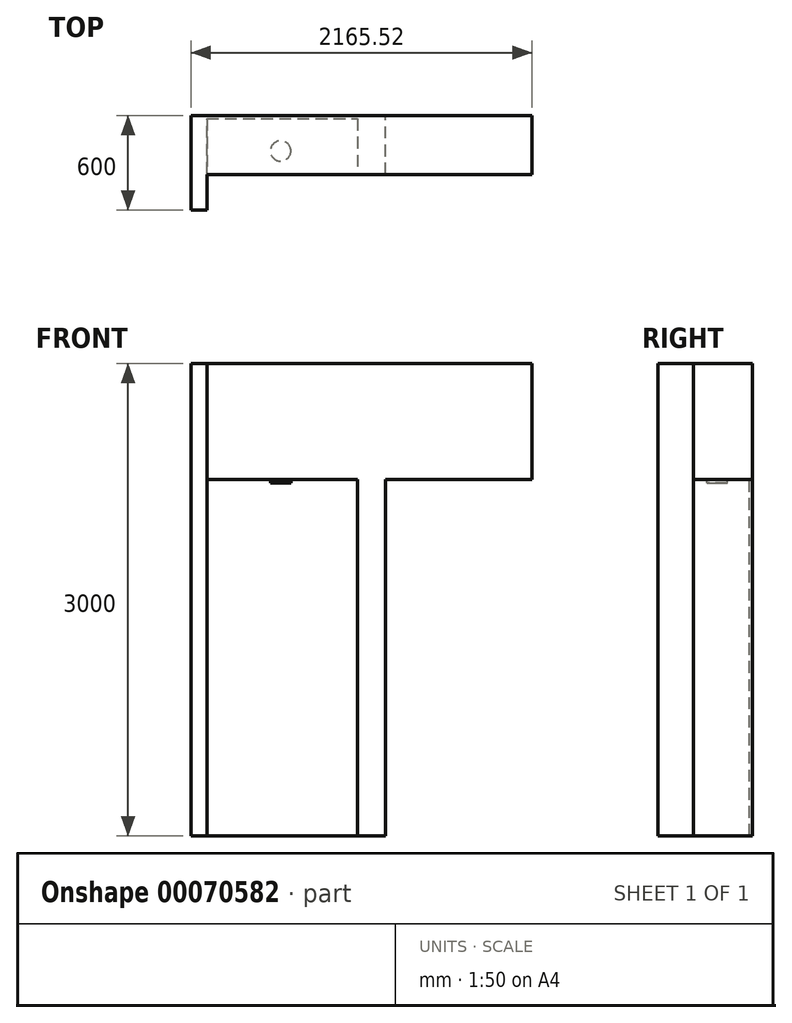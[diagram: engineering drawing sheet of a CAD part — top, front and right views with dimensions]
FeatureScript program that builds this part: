
annotation { "Feature Type Name" : "Feature", "Feature Type Description" : "" }
export const myFeature = defineFeature(function(context is Context, id is Id, definition is map)
    precondition{}
    {
        {
            var Q0;
            Q0=qCreatedBy(makeId("Front.planeOp"),FACE);
            var sketch = newSketch(context, id + "F0", { "sketchPlane" : qUnion([Q0])});
            skLineSegment(sketch, "E0.bottom", {"start": v(-617.5, 0) * mm, "end": v(617.5, 0) * mm});
            skLineSegment(sketch, "E0.top", {"start": v(-617.5, 3000) * mm, "end": v(1548.02, 3000) * mm});
            skLineSegment(sketch, "E0.left", {"start": v(-617.5, 0) * mm, "end": v(-617.5, 3000) * mm});
            skLineSegment(sketch, "E0.right", {"start": v(617.5, 0) * mm, "end": v(617.5, 2263) * mm});
            skLineSegment(sketch, "E1", {"start": v(617.5, 2263) * mm, "end": v(1548.02, 2263) * mm});
            skLineSegment(sketch, "E2", {"start": v(1548.02, 2263) * mm, "end": v(1548.02, 3000) * mm});
            skSolve(sketch);
        }
        {
            var Q0;
            Q0=makeQuery(id+"F0.imprint","IMPRINT",FACE,{"disambiguationData":[TD([[makeQuery(id+"F0.imprint","IMPRINT",EDGE,{"derivedFrom":sQuery(id+"F0.wireOp",EDGE,"E0.bottom")}),1.0]])]});
            extrude(context, id + "F1", {"entities" : qUnion([Q0]), "depth" : 600 * mm});
        }
        {
            var Q0;
            Q0=makeQuery(id+"F1.opExtrude","SWEPT_FACE",FACE,{"disambiguationData":[OSD([sQuery(id+"F0.wireOp",EDGE,"E0.top")])]});
            var sketch = newSketch(context, id + "F2", { "sketchPlane" : qUnion([Q0])});
            skLineSegment(sketch, "E3.bottom", {"start": v(-517.5, -600) * mm, "end": v(1548.02, -600) * mm});
            skLineSegment(sketch, "E3.top", {"start": v(-517.5, -374.12) * mm, "end": v(1548.02, -374.12) * mm});
            skLineSegment(sketch, "E3.left", {"start": v(-517.5, -600) * mm, "end": v(-517.5, -374.12) * mm});
            skLineSegment(sketch, "E3.right", {"start": v(1548.02, -600) * mm, "end": v(1548.02, -374.12) * mm});
            skSolve(sketch);
        }
        {
            var Q0;
            Q0=makeQuery(id+"F2.imprint","IMPRINT",FACE,{"disambiguationData":[TD([[makeQuery(id+"F2.imprint","IMPRINT",EDGE,{"derivedFrom":sQuery(id+"F2.wireOp",EDGE,"E3.bottom")}),1.0]])]});
            extrude(context, id + "F3", {"entities" : qUnion([Q0]), "operationType" : NewBodyOperationType.REMOVE, "oppositeDirection" : true, "depth" : 4000 * mm});
        }
        {
            var Q0;
            Q0=makeQuery(id+"F3.boolean.opBoolean","COPY",FACE,{"derivedFrom":makeQuery(id+"F3.opExtrude","SWEPT_FACE",FACE,{"disambiguationData":[OSD([sQuery(id+"F2.wireOp",EDGE,"E3.top")])]})});
            var sketch = newSketch(context, id + "F4", { "sketchPlane" : qUnion([Q0])});
            skLineSegment(sketch, "E4.bottom", {"start": v(-517.5, 0) * mm, "end": v(440.5, 0) * mm});
            skLineSegment(sketch, "E4.top", {"start": v(-517.5, 2263) * mm, "end": v(440.5, 2263) * mm});
            skLineSegment(sketch, "E4.left", {"start": v(-517.5, 0) * mm, "end": v(-517.5, 2263) * mm});
            skLineSegment(sketch, "E4.right", {"start": v(440.5, 0) * mm, "end": v(440.5, 2263) * mm});
            skSolve(sketch);
        }
        {
            var Q0;
            Q0=makeQuery(id+"F4.imprint","IMPRINT",FACE,{"disambiguationData":[TD([[makeQuery(id+"F4.imprint","IMPRINT",EDGE,{"derivedFrom":sQuery(id+"F4.wireOp",EDGE,"E4.bottom")}),1.0]])]});
            extrude(context, id + "F5", {"entities" : qUnion([Q0]), "operationType" : NewBodyOperationType.REMOVE, "oppositeDirection" : true, "depth" : 355 * mm});
        }
        {
            var Q0;
            Q0=makeQuery(id+"F5.boolean.opBoolean","COPY",FACE,{"derivedFrom":makeQuery(id+"F5.opExtrude","SWEPT_FACE",FACE,{"disambiguationData":[OSD([sQuery(id+"F4.wireOp",EDGE,"E4.top")])]})});
            var sketch = newSketch(context, id + "F6", { "sketchPlane" : qUnion([Q0])});
            skCircle(sketch, "E5", {"center": v(-48.5, 224.12) * mm, "radius": 65 * mm});
            skSolve(sketch);
        }
        {
            var Q0;
            Q0 = qSketchRegion(id + "F6", true);
            extrude(context, id + "F7", {"entities" : qUnion([Q0]), "operationType" : NewBodyOperationType.ADD, "depth" : 22 * mm});
        }
    });
